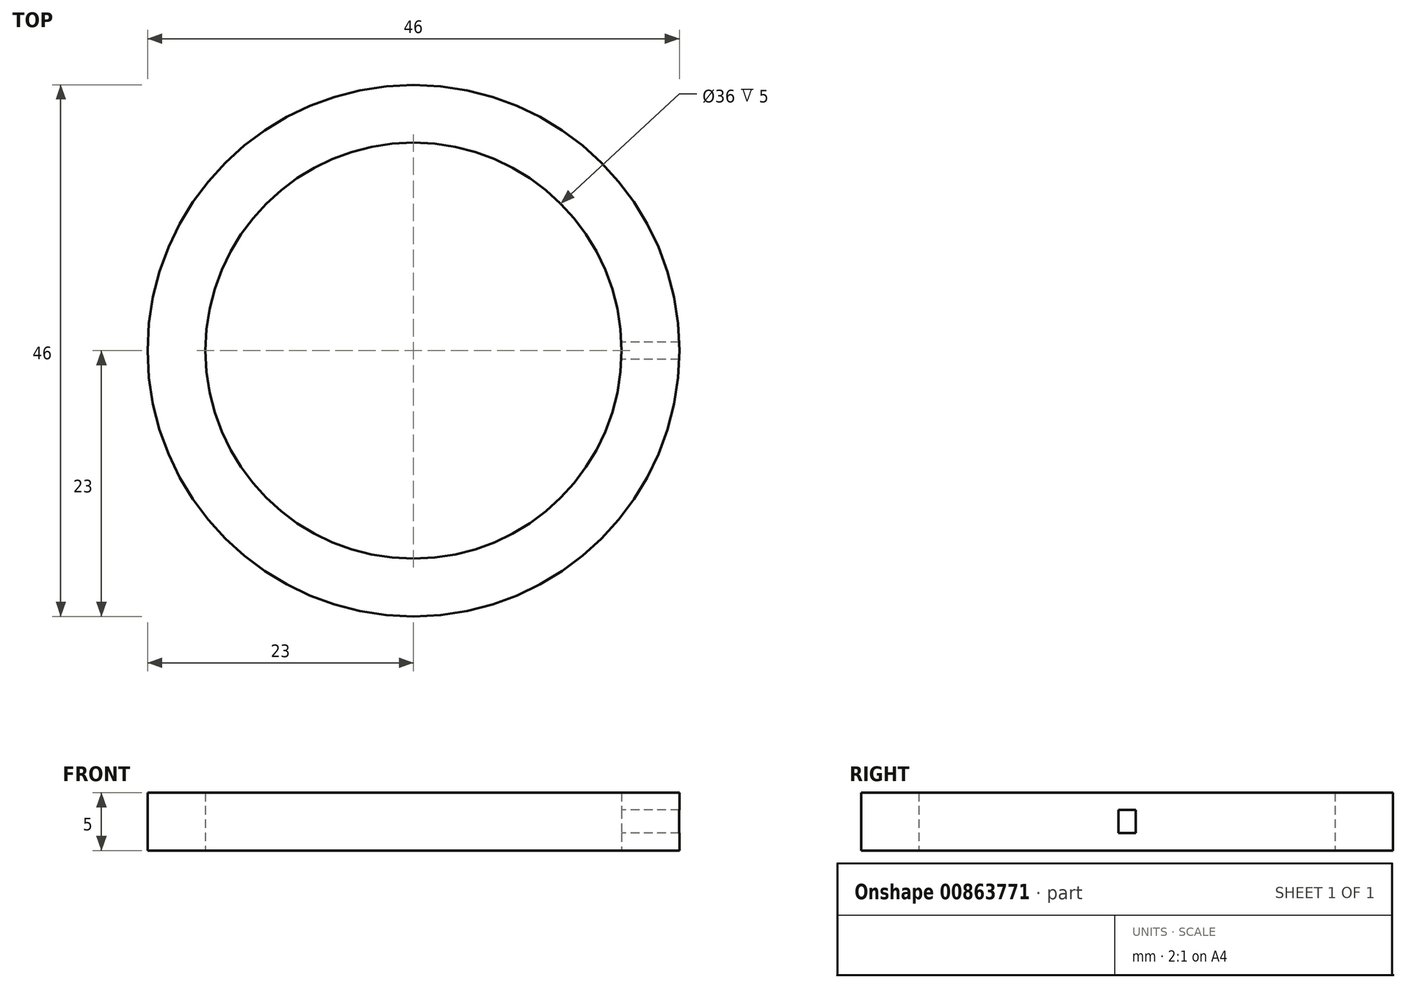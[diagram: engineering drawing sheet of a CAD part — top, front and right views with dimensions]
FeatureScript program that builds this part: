
annotation { "Feature Type Name" : "Feature", "Feature Type Description" : "" }
export const myFeature = defineFeature(function(context is Context, id is Id, definition is map)
    precondition{}
    {
        {
            var Q0;
            Q0=qCreatedBy(makeId("Top.planeOp"),FACE);
            var sketch = newSketch(context, id + "F0", { "sketchPlane" : qUnion([Q0])});
            skCircle(sketch, "E0", {"center": v(0, 0) * mm, "radius": 18 * mm});
            skCircle(sketch, "E1", {"center": v(0, 0) * mm, "radius": 23 * mm});
            skSolve(sketch);
        }
        {
            var Q0;
            Q0=makeQuery(id+"F0.imprint","IMPRINT",FACE,{"disambiguationData":[TD([[makeQuery(id+"F0.imprint","IMPRINT",EDGE,{"derivedFrom":sQuery(id+"F0.wireOp",EDGE,"E0")}),-1.0]])]});
            extrude(context, id + "F1", {"entities" : qUnion([Q0]), "depth" : 5 * mm, "offsetDistance" : 25 * mm});
        }
        {
            var Q0;
            Q0=qCreatedBy(makeId("Right.planeOp"),FACE);
            var sketch = newSketch(context, id + "F2", { "sketchPlane" : qUnion([Q0])});
            skLineSegment(sketch, "E2", {"start": v(-23, 0) * mm, "end": v(-23, 5) * mm});
            skLineSegment(sketch, "E3", {"start": v(23, 5) * mm, "end": v(23, 0) * mm});
            skLineSegment(sketch, "E4.bottom", {"start": v(-0.75, 3.5) * mm, "end": v(0.75, 3.5) * mm});
            skLineSegment(sketch, "E4.top", {"start": v(-0.75, 1.5) * mm, "end": v(0.75, 1.5) * mm});
            skLineSegment(sketch, "E4.left", {"start": v(-0.75, 3.5) * mm, "end": v(-0.75, 1.5) * mm});
            skLineSegment(sketch, "E4.right", {"start": v(0.75, 3.5) * mm, "end": v(0.75, 1.5) * mm});
            skSolve(sketch);
        }
        {
            var Q0;
            Q0=makeQuery(id+"F2.imprint","IMPRINT",FACE,{"disambiguationData":[TD([[makeQuery(id+"F2.imprint","IMPRINT",EDGE,{"derivedFrom":sQuery(id+"F2.wireOp",EDGE,"E4.bottom")}),-1.0]])]});
            extrude(context, id + "F3", {"entities" : qUnion([Q0]), "operationType" : NewBodyOperationType.REMOVE, "endBound" : BoundingType.THROUGH_ALL, "depth" : 25 * mm, "offsetDistance" : 25 * mm});
        }
        {
            var Q0;
            Q0=qCreatedBy(makeId("Front.planeOp"),FACE);
            var sketch = newSketch(context, id + "F4", { "sketchPlane" : qUnion([Q0])});
            skLineSegment(sketch, "E5", {"start": v(0, 0) * mm, "end": v(0, 10.48) * mm});
            skSolve(sketch);
        }
    });
